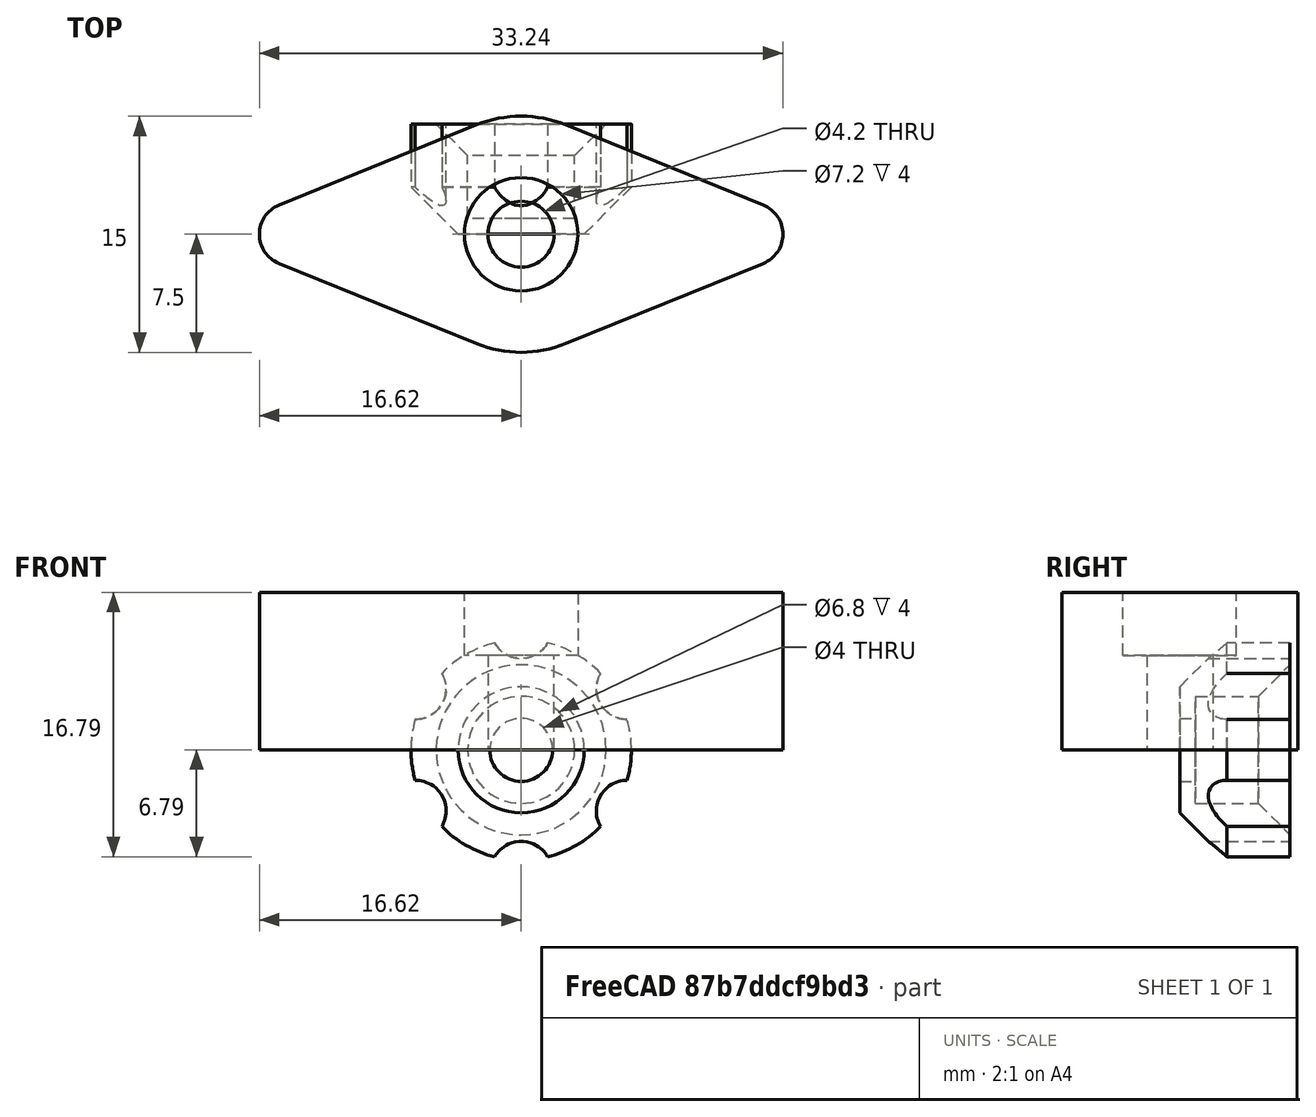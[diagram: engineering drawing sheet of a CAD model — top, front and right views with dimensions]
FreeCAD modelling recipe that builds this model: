
FCSTD DOCUMENT  (FreeCAD 0.19R)
Label: M4Knob
License: All rights reserved
LicenseURL: http://en.wikipedia.org/wiki/All_rights_reserved
objects: Sketcher::SketchObject×4, PartDesign::Pocket×2, PartDesign::Body×2, PartDesign::Pad×1, PartDesign::Revolution×1, PartDesign::Chamfer×1, PartDesign::PolarPattern×1, Mesh::Feature×1
note: 17 computed .brp shape members not serialized (recipe doc carries the construction recipe); baked Part::Feature solids carry a one-line shape summary decoded from their .brp

FEATURE [Sketcher::SketchObject] Sketch
  FullyConstrained = false
  MapMode = 5
  Support = -> [XY_Plane]
  sketch-geometry (9):
    g0: ArcOfCircle CenterX=0 CenterY=0 CenterZ=0 NormalX=0 NormalY=0 NormalZ=1 AngleXU=0 Radius=7.5 StartAngle=1.18524 EndAngle=1.95635
    g1: ArcOfCircle CenterX=0 CenterY=0 CenterZ=0 NormalX=0 NormalY=0 NormalZ=1 AngleXU=0 Radius=7.5 StartAngle=4.32683 EndAngle=5.09795
    g2: ArcOfCircle CenterX=-14.6247 CenterY=0 CenterZ=0 NormalX=0 NormalY=0 NormalZ=1 AngleXU=0 Radius=2 StartAngle=1.95635 EndAngle=4.32683
    g3: ArcOfCircle CenterX=14.6247 CenterY=0 CenterZ=0 NormalX=0 NormalY=0 NormalZ=1 AngleXU=0 Radius=2 StartAngle=5.09795 EndAngle=7.46842
    g4: LineSegment StartX=-15.3768 StartY=1.85318 StartZ=0 EndX=-2.82057 EndY=6.94942 EndZ=0
    g5: LineSegment StartX=2.82057 StartY=6.94942 StartZ=0 EndX=15.3768 EndY=1.85318 EndZ=0
    g6: LineSegment StartX=15.3768 StartY=-1.85318 StartZ=0 EndX=2.82057 EndY=-6.94942 EndZ=0
    g7: LineSegment StartX=-15.3768 StartY=-1.85318 StartZ=0 EndX=-2.82057 EndY=-6.94942 EndZ=0
    g8: Circle CenterX=0 CenterY=0 CenterZ=0 NormalX=0 NormalY=0 NormalZ=1 AngleXU=0 Radius=2.1
  constraints (17):
    c: Coincident(g1,g0)
    c: PointOnObject(g2,g-1)
    c: Tangent(g7,g1) = -1.5708
    c: Tangent(g6,g1) = 1.5708
    c: Tangent(g6,g3) = 1.5708
    c: Tangent(g5,g3) = 1.5708
    c: Tangent(g5,g0) = 1.5708
    c: Tangent(g4,g0) = 1.5708
    c: Tangent(g4,g2) = 1.5708
    c: Tangent(g7,g2) = -1.5708
    c: Symmetric(g3,g2,g-2)
    c: Diameter(g3) = 4
    c: Coincident(g8,g0)
    c: Diameter(g8) = 4.2
    c: Coincident(g0,g-1)
    c: Symmetric(g1,g0,g0)
    c: Distance(g0,g1) = 15
FEATURE [PartDesign::Pad] Pad
  Direction = (1,1,1)
  Length = 10
  Length2 = 100
  Profile = -> Sketch
  Type = 0
FEATURE [Sketcher::SketchObject] Sketch001
  FullyConstrained = true
  MapMode = 5
  Placement = pos=(0,0,10) rot=(0,0,1;0rad)
  Support = -> [Pad]
  sketch-geometry (1):
    g0: Circle CenterX=0 CenterY=0 CenterZ=0 NormalX=0 NormalY=0 NormalZ=1 AngleXU=0 Radius=3.6
  constraints (2):
    c: Coincident(g0,g-1)
    c: Diameter(g0) = 7.2
FEATURE [PartDesign::Pocket] Pocket
  BaseFeature = -> Pad
  Length = 4
  Length2 = 100
  Profile = -> Sketch001
  Type = 0
FEATURE [PartDesign::Body] Body  label="knob1"
  Group = -> [Sketch,Pad,Sketch001,Pocket]
  Origin = -> Origin
  Tip = -> Pocket
FEATURE [Sketcher::SketchObject] Sketch002
  FullyConstrained = true
  MapMode = 5
  Support = -> [XY_Plane001]
  sketch-geometry (7):
    g0: LineSegment StartX=2 StartY=0 StartZ=0 EndX=2 EndY=1 EndZ=0
    g1: LineSegment StartX=2 StartY=1 StartZ=0 EndX=3.4 EndY=1 EndZ=0
    g2: LineSegment StartX=3.4 StartY=1 StartZ=0 EndX=3.4 EndY=7 EndZ=0
    g3: LineSegment StartX=3.4 StartY=7 StartZ=0 EndX=7 EndY=7 EndZ=0
    g4: LineSegment StartX=7 StartY=7 StartZ=0 EndX=7 EndY=3 EndZ=0
    g5: LineSegment StartX=7 StartY=3 StartZ=0 EndX=4 EndY=0 EndZ=0
    g6: LineSegment StartX=4 StartY=0 StartZ=0 EndX=2 EndY=0 EndZ=0
  constraints (21):
    c: PointOnObject(g0,g-1)
    c: Vertical(g0)
    c: Coincident(g0,g1)
    c: Horizontal(g1)
    c: Coincident(g1,g2)
    c: Vertical(g2)
    c: Coincident(g2,g3)
    c: Horizontal(g3)
    c: Coincident(g3,g4)
    c: Vertical(g4)
    c: Coincident(g4,g5)
    c: PointOnObject(g5,g-1)
    c: Coincident(g5,g6)
    c: Coincident(g6,g0)
    c: DistanceX(g0) = 2
    c: DistanceX(g1) = 3.4
    c: Distance(g2) = 6
    c: Distance(g0) = 1
    c: DistanceX(g3) = 7
    c: Angle(g5) = -2.35619
    c: DistanceX(g5) = 4
FEATURE [PartDesign::Revolution] Revolution
  Angle = 360
  Axis = (0,1,0)
  Base = (0,0,0)
  Profile = -> Sketch002
  ReferenceAxis = -> Sketch002 [V_Axis]
  Reversed = true
FEATURE [PartDesign::Chamfer] Chamfer
  Angle = 45
  Base = -> Revolution [Edge5]
  BaseFeature = -> Revolution
  ChamferType = 0
  FlipDirection = false
  Size = 2
  Size2 = 1
  SupportTransform = false
FEATURE [Sketcher::SketchObject] Sketch003
  FullyConstrained = false
  MapMode = 5
  Placement = pos=(0,7,0) rot=(0,0.707107,0.707107;3.14159rad)
  Support = -> [Chamfer]
  sketch-geometry (1):
    g0: Circle CenterX=0 CenterY=7.74927 CenterZ=0 NormalX=0 NormalY=0 NormalZ=1 AngleXU=0 Radius=1.93916
  constraints (1):
    c: PointOnObject(g0,g-2)
FEATURE [PartDesign::Pocket] Pocket001
  BaseFeature = -> Chamfer
  Length = 5
  Length2 = 100
  Profile = -> Sketch003
  Type = 1
FEATURE [PartDesign::PolarPattern] PolarPattern
  Angle = 360
  Axis = -> Sketch003 [N_Axis]
  BaseFeature = -> Pocket001
  Occurrences = 6
  Originals = -> [Pocket001]
FEATURE [PartDesign::Body] Body001  label="Knob2"
  Group = -> [Sketch002,Revolution,Chamfer,Sketch003,Pocket001,PolarPattern]
  Origin = -> Origin001
  Tip = -> PolarPattern
FEATURE [Mesh::Feature] Mesh  label="PolarPattern (Meshed)"
